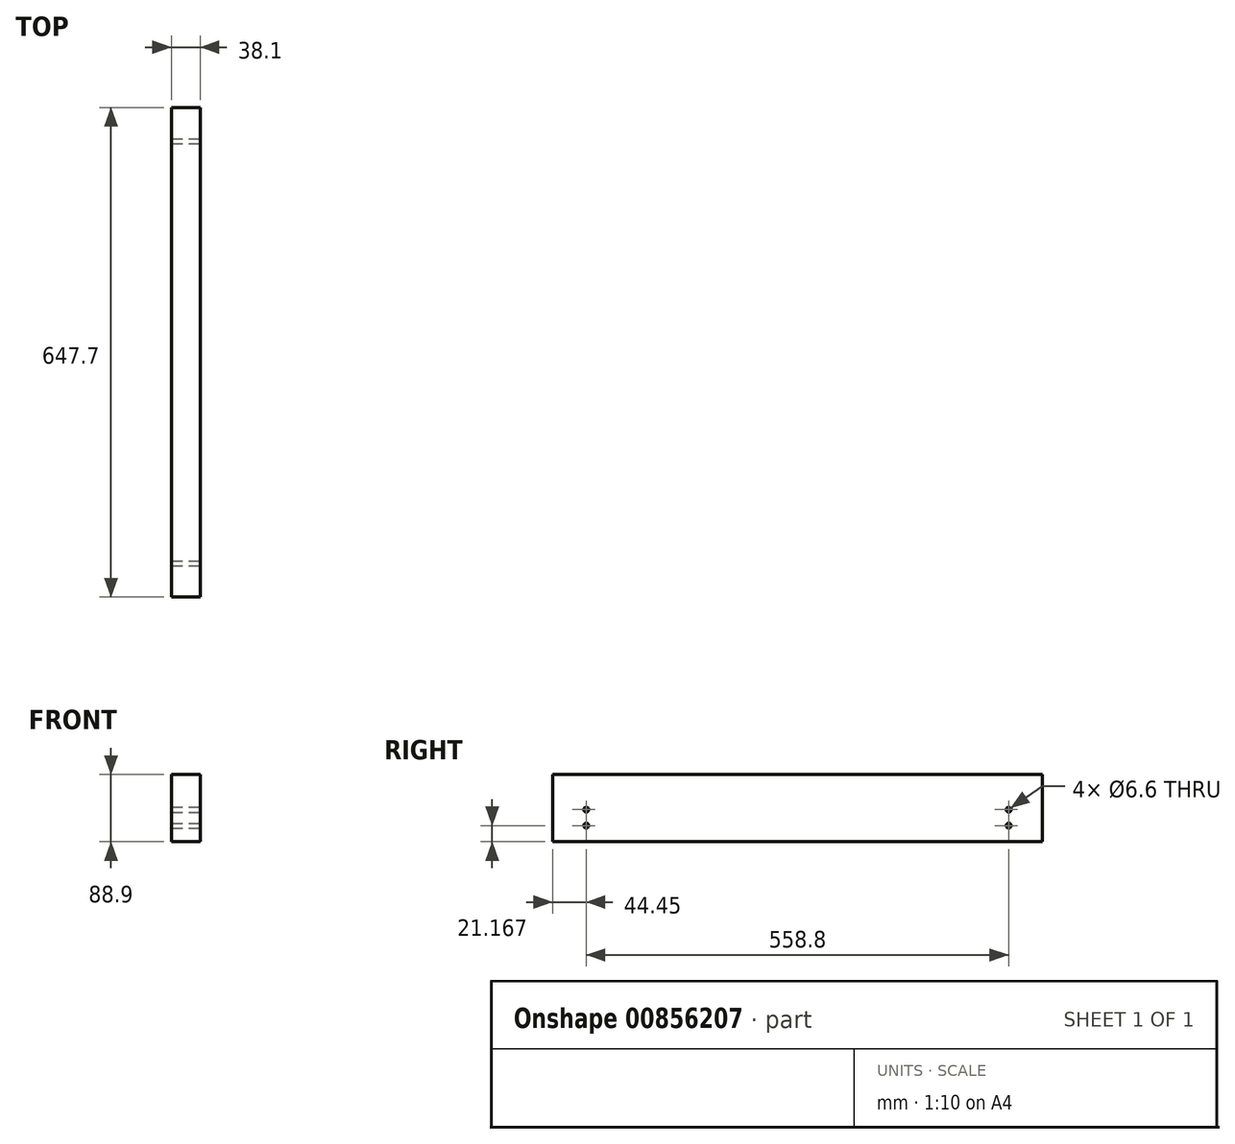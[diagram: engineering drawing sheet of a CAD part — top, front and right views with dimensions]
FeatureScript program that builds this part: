
annotation { "Feature Type Name" : "Feature", "Feature Type Description" : "" }
export const myFeature = defineFeature(function(context is Context, id is Id, definition is map)
    precondition{}
    {
        {
            var Q0;
            Q0=qCreatedBy(makeId("Front.planeOp"),FACE);
            var sketch = newSketch(context, id + "F0", { "sketchPlane" : qUnion([Q0])});
            skLineSegment(sketch, "E0.bottom", {"start": v(19.05, 44.45) * mm, "end": v(-19.05, 44.45) * mm});
            skLineSegment(sketch, "E0.top", {"start": v(19.05, -44.45) * mm, "end": v(-19.05, -44.45) * mm});
            skLineSegment(sketch, "E0.left", {"start": v(19.05, 44.45) * mm, "end": v(19.05, -44.45) * mm});
            skLineSegment(sketch, "E0.right", {"start": v(-19.05, 44.45) * mm, "end": v(-19.05, -44.45) * mm});
            skPoint(sketch, "E0.middle", {"position": v(0, 0) * mm});
            skSolve(sketch);
        }
        {
            var Q0;
            Q0=makeQuery(id+"F0.imprint","IMPRINT",FACE,{"disambiguationData":[TD([[makeQuery(id+"F0.imprint","IMPRINT",EDGE,{"derivedFrom":sQuery(id+"F0.wireOp",EDGE,"E0.bottom")}),1.0]])]});
            extrude(context, id + "F1", {"entities" : qUnion([Q0]), "depth" : 647.7 * mm, "offsetDistance" : 25.4 * mm});
        }
        {
            var Q0;
            Q0=makeQuery(id+"F1.opExtrude","SWEPT_FACE",FACE,{"disambiguationData":[OSD([sQuery(id+"F0.wireOp",EDGE,"E0.left")])]});
            var sketch = newSketch(context, id + "F2", { "sketchPlane" : qUnion([Q0])});
            skLineSegment(sketch, "E1", {"start": v(-558.8, 44.45) * mm, "end": v(-558.8, -44.45) * mm, "construction": true});
            skLineSegment(sketch, "E2", {"start": v(-647.7, 19.05) * mm, "end": v(-558.8, 19.05) * mm, "construction": true});
            skLineSegment(sketch, "E3", {"start": v(-603.25, -44.45) * mm, "end": v(-603.25, 19.05) * mm, "construction": true});
            skPoint(sketch, "E3.endSnap0", {"position": v(-603.25, 19.05) * mm});
            skCircle(sketch, "E4", {"center": v(-603.25, -2.12) * mm, "radius": 3.3 * mm});
            skCircle(sketch, "E5", {"center": v(-603.25, -23.28) * mm, "radius": 3.3 * mm});
            skLineSegment(sketch, "E6", {"start": v(-88.9, 44.45) * mm, "end": v(-88.9, -44.45) * mm, "construction": true});
            skLineSegment(sketch, "E7", {"start": v(-88.9, 19.05) * mm, "end": v(0, 19.05) * mm, "construction": true});
            skLineSegment(sketch, "E8", {"start": v(-44.45, 19.05) * mm, "end": v(-44.45, -44.45) * mm, "construction": true});
            skCircle(sketch, "E9", {"center": v(-44.45, -23.28) * mm, "radius": 3.3 * mm});
            skCircle(sketch, "E10", {"center": v(-44.45, -2.12) * mm, "radius": 3.3 * mm});
            skSolve(sketch);
        }
        {
            var Q0;
            Q0 = qSketchRegion(id + "F2", true);
            extrude(context, id + "F3", {"entities" : qUnion([Q0]), "operationType" : NewBodyOperationType.REMOVE, "endBound" : BoundingType.THROUGH_ALL, "oppositeDirection" : true, "depth" : 25.4 * mm, "offsetDistance" : 25.4 * mm});
        }
    });
